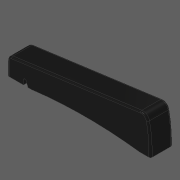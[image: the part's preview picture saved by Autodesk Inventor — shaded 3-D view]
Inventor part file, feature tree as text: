
AUTODESK INVENTOR PART (.ipt)
format: ipt  version: 2020 (Build 240168000, 168)  size: 275,456 bytes
history: native  units: in
note: dims shown in document units (in); Inventor stores cm internally (conversion verified against a paired STEP export)
features: other x4, extrude x3, fillet x2
ambient origin geometry x8: Origin, YZ Plane, XZ Plane, XY Plane, X Axis, Y Axis, Z Axis, Center Point
bodies: Solid1 (feature_tree)
feature tree (9):
  other  "BlackKey0"
  other  "Slot Start Plane"
  other  "Key Profile"
  extrude  "Key"  Depth=0.0787in
  extrude  "Protrusion Cutout"  TaperAngle=0.0deg  [1 undecoded]
  fillet  "Front Fillet"  [1 undecoded]
  extrude  "Slot"  Depth=0.1181in
  fillet  "Edge Softening"  Radius=0.1374in
  other  "Slot Sketch"
note: 2 required parameter values undecoded (feature->parameter linkage not recoverable at this tier; creation-order binding heuristic only, values carry confidence <= 0.55)
